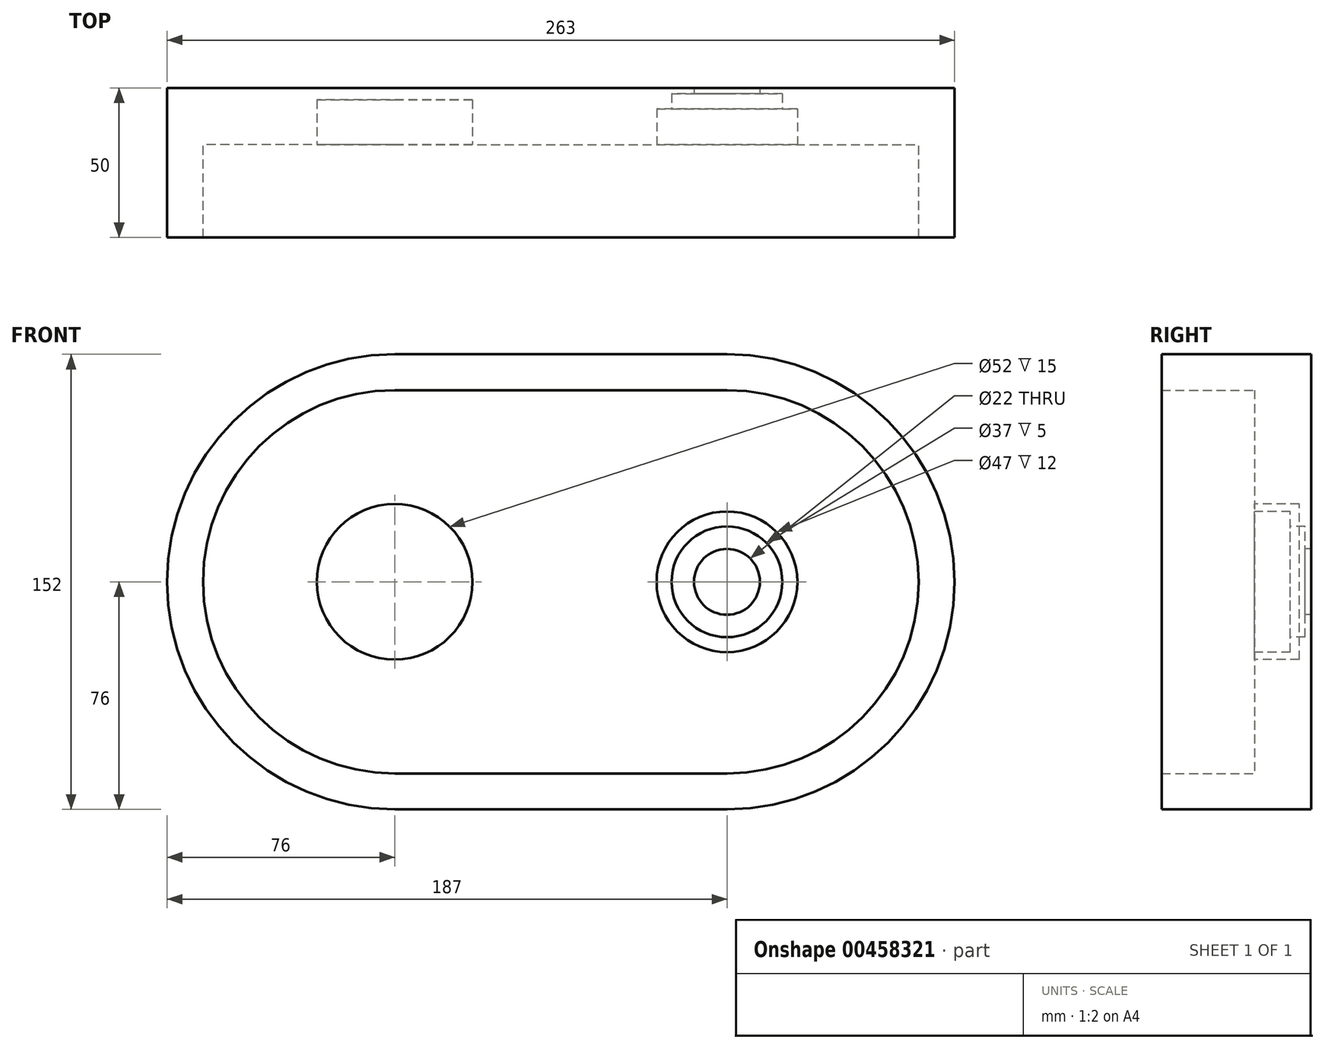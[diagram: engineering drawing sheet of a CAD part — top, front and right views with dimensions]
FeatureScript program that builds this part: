
annotation { "Feature Type Name" : "Feature", "Feature Type Description" : "" }
export const myFeature = defineFeature(function(context is Context, id is Id, definition is map)
    precondition{}
    {
        {
            var Q0;
            Q0=qCreatedBy(makeId("Front.planeOp"),FACE);
            var sketch = newSketch(context, id + "F0", { "sketchPlane" : qUnion([Q0])});
            skArc(sketch, "E0", {"start": v(0, 76) * mm, "mid": v(-76, 0) * mm, "end": v(0, -76) * mm});
            skLineSegment(sketch, "E1", {"start": v(0, 76) * mm, "end": v(111, 76) * mm});
            skLineSegment(sketch, "E2", {"start": v(0, -76) * mm, "end": v(111, -76) * mm});
            skPoint(sketch, "E3.center.orphan", {"position": v(111, 0) * mm});
            skArc(sketch, "E4", {"start": v(111, -76) * mm, "mid": v(187, 0) * mm, "end": v(111, 76) * mm});
            skSolve(sketch);
        }
        {
            var Q0;
            Q0=qCreatedBy(makeId("Front.planeOp"),FACE);
            cPlane(context, id + "F1", {"entities" : qUnion([Q0]), "cplaneType" : CPlaneType.OFFSET, "offset" : 19 * mm, "width" : 150 * mm, "height" : 150 * mm});
        }
        {
            var Q0;
            Q0 = qSketchRegion(id + "F0", true);
            var Q1;
            Q1=makeQuery(id+"F0.imprint","IMPRINT",FACE,{"disambiguationData":[TD([[makeQuery(id+"F0.imprint","IMPRINT",EDGE,{"derivedFrom":sQuery(id+"F0.wireOp",EDGE,"E0")}),1.0]])]});
            extrude(context, id + "F2", {"entities" : qUnion([Q0, Q1]), "depth" : 50 * mm, "offsetDistance" : 25 * mm});
        }
        {
            var Q0;
            Q0=qCreatedBy(id+"F1.planeOp",FACE);
            var sketch = newSketch(context, id + "F3", { "sketchPlane" : qUnion([Q0])});
            skArc(sketch, "E5", {"start": v(0, 64) * mm, "mid": v(-64, 0) * mm, "end": v(0, -64) * mm});
            skArc(sketch, "E6", {"start": v(111, -64) * mm, "mid": v(175, 0) * mm, "end": v(111, 64) * mm});
            skLineSegment(sketch, "E7", {"start": v(0, 64) * mm, "end": v(111, 64) * mm});
            skLineSegment(sketch, "E8", {"start": v(0, -64) * mm, "end": v(111, -64) * mm});
            skSolve(sketch);
        }
        {
            var Q0;
            Q0=makeQuery(id+"F3.imprint","IMPRINT",FACE,{"disambiguationData":[TD([[makeQuery(id+"F3.imprint","IMPRINT",EDGE,{"derivedFrom":sQuery(id+"F3.wireOp",EDGE,"E5")}),1.0]])]});
            extrude(context, id + "F4", {"entities" : qUnion([Q0]), "operationType" : NewBodyOperationType.REMOVE, "depth" : 31 * mm, "offsetDistance" : 25 * mm});
        }
        {
            var Q0;
            Q0=qCreatedBy(id+"F1.planeOp",FACE);
            var sketch = newSketch(context, id + "F5", { "sketchPlane" : qUnion([Q0])});
            skCircle(sketch, "E9", {"center": v(0, 0) * mm, "radius": 26 * mm});
            skSolve(sketch);
        }
        {
            var Q0;
            Q0 = qSketchRegion(id + "F5", true);
            var Q1;
            Q1=makeQuery(id+"F5.imprint","IMPRINT",FACE,{"disambiguationData":[TD([[makeQuery(id+"F5.imprint","IMPRINT",EDGE,{"derivedFrom":sQuery(id+"F5.wireOp",EDGE,"E9")}),1.0]])]});
            extrude(context, id + "F6", {"entities" : qUnion([Q0, Q1]), "operationType" : NewBodyOperationType.REMOVE, "oppositeDirection" : true, "depth" : 15 * mm, "offsetDistance" : 25 * mm});
        }
        {
            var Q0;
            Q0=qCreatedBy(makeId("Right.planeOp"),FACE);
            cPlane(context, id + "F7", {"entities" : qUnion([Q0]), "cplaneType" : CPlaneType.OFFSET, "offset" : 111 * mm, "width" : 150 * mm, "height" : 150 * mm});
        }
        {
            var Q0;
            Q0=qCreatedBy(id+"F7.planeOp",FACE);
            var sketch = newSketch(context, id + "F8", { "sketchPlane" : qUnion([Q0])});
            skLineSegment(sketch, "E10", {"start": v(0, 0) * mm, "end": v(-19, 0) * mm});
            skCircle(sketch, "E11", {"center": v(0, 0) * mm, "radius": 23.5 * mm, "construction": true});
            skLineSegment(sketch, "E12", {"start": v(0, 23.5) * mm, "end": v(-22.35, 23.5) * mm, "construction": true});
            skLineSegment(sketch, "E13", {"start": v(-19, 0) * mm, "end": v(-19, 23.5) * mm});
            skCircle(sketch, "E14", {"center": v(0, 0) * mm, "radius": 18.5 * mm, "construction": true});
            skLineSegment(sketch, "E15", {"start": v(-19, 23.5) * mm, "end": v(-7, 23.5) * mm});
            skLineSegment(sketch, "E16", {"start": v(-7, 23.5) * mm, "end": v(-7, 15.08) * mm, "construction": true});
            skLineSegment(sketch, "E17", {"start": v(-7, 18.5) * mm, "end": v(-7, 23.5) * mm});
            skCircle(sketch, "E18", {"center": v(0, 0) * mm, "radius": 11 * mm, "construction": true});
            skLineSegment(sketch, "E19", {"start": v(-7, 18.5) * mm, "end": v(-2, 18.5) * mm});
            skLineSegment(sketch, "E20", {"start": v(-2, 18.5) * mm, "end": v(-2, 11) * mm});
            skLineSegment(sketch, "E21", {"start": v(0, 11) * mm, "end": v(-2, 11) * mm});
            skPoint(sketch, "E22.orphan", {"position": v(-2, 10.82) * mm});
            skLineSegment(sketch, "E23", {"start": v(0, 11) * mm, "end": v(0, 0) * mm});
            skLineSegment(sketch, "E24.MirrorCS", {"start": v(-19, 0) * mm, "end": v(-19, -23.5) * mm});
            skLineSegment(sketch, "E25.MirrorCS", {"start": v(0, -23.5) * mm, "end": v(-22.35, -23.5) * mm, "construction": true});
            skLineSegment(sketch, "E26.MirrorCS", {"start": v(-7, -23.5) * mm, "end": v(-7, -15.08) * mm, "construction": true});
            skLineSegment(sketch, "E27.MirrorCS", {"start": v(-7, -18.5) * mm, "end": v(-2, -18.5) * mm});
            skLineSegment(sketch, "E28.MirrorCS", {"start": v(-2, -18.5) * mm, "end": v(-2, -11) * mm});
            skLineSegment(sketch, "E29.MirrorCS", {"start": v(0, -11) * mm, "end": v(-2, -11) * mm});
            skLineSegment(sketch, "E30.MirrorCS", {"start": v(0, -11) * mm, "end": v(0, 0) * mm});
            skLineSegment(sketch, "E31", {"start": v(0, 0) * mm, "end": v(-28.58, 0) * mm, "construction": true});
            skSolve(sketch);
        }
        {
            var Q0;
            Q0 = qSketchRegion(id + "F8", true);
            var Q1;
            Q1=sQuery(id+"F8.wireOp",EDGE,"E10");
            revolve(context, id + "F9", {"operationType" : NewBodyOperationType.REMOVE, "entities" : qUnion([Q0]), "axis" : qUnion([Q1]), "revolveType" : RevolveType.SYMMETRIC, "oppositeDirection" : true, "angle" : 360 * degree});
        }
    });
